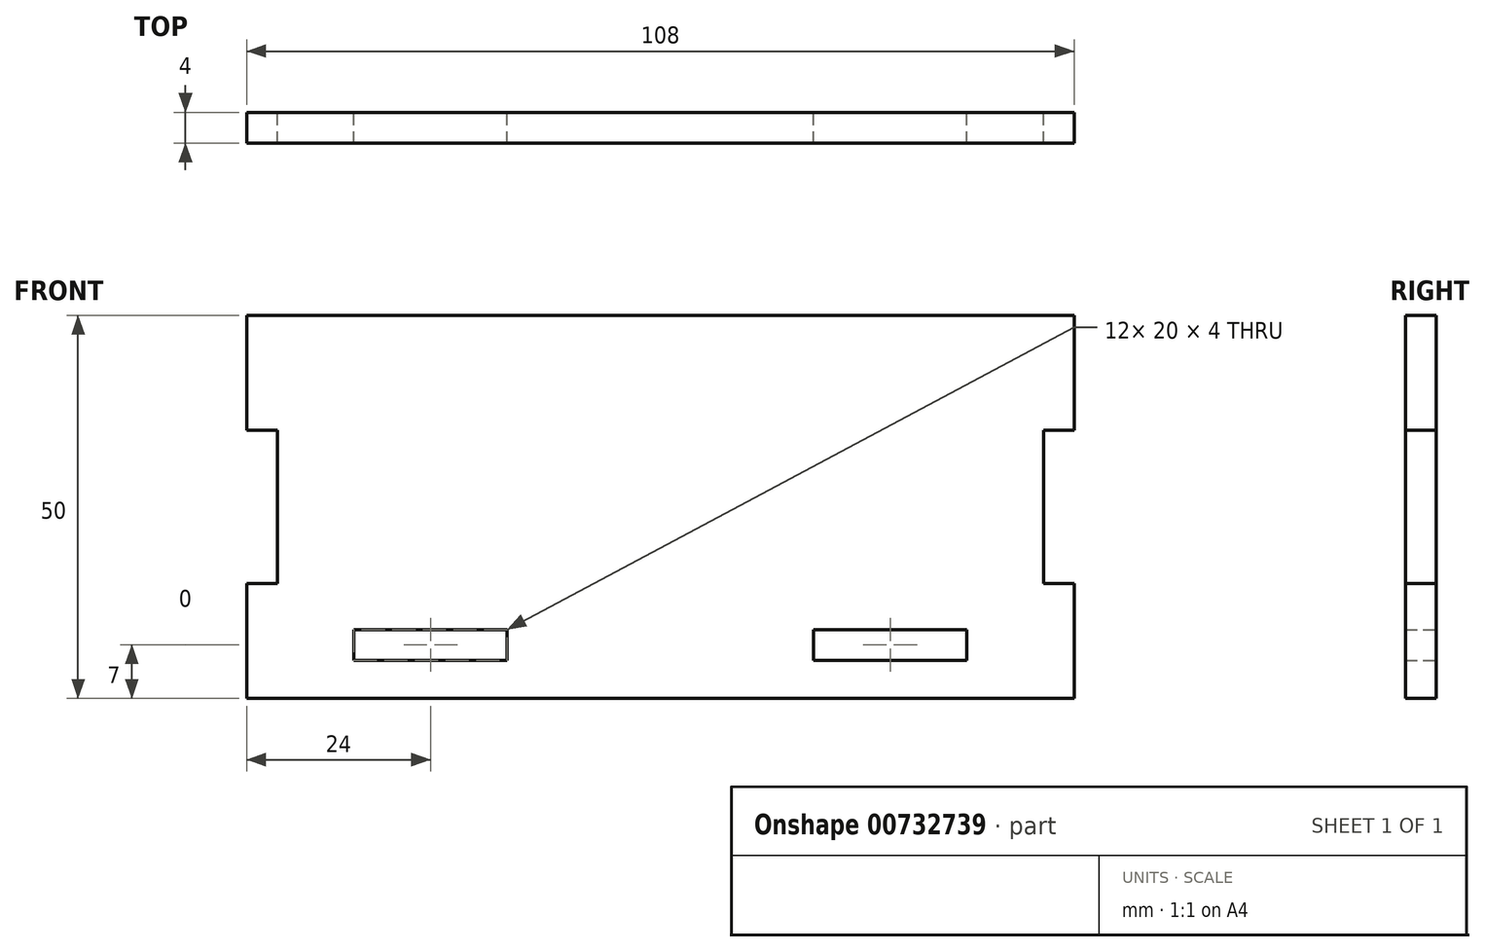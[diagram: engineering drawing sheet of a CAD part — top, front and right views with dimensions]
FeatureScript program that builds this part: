
annotation { "Feature Type Name" : "Feature", "Feature Type Description" : "" }
export const myFeature = defineFeature(function(context is Context, id is Id, definition is map)
    precondition{}
    {
        {
            var Q0;
            Q0=qCreatedBy(makeId("Front.planeOp"),FACE);
            var sketch = newSketch(context, id + "F0", { "sketchPlane" : qUnion([Q0])});
            skLineSegment(sketch, "E0.bottom", {"start": v(54, 25) * mm, "end": v(-54, 25) * mm});
            skLineSegment(sketch, "E0.top", {"start": v(54, -25) * mm, "end": v(-54, -25) * mm});
            skLineSegment(sketch, "E0.left", {"start": v(54, 25) * mm, "end": v(54, 10) * mm});
            skLineSegment(sketch, "E0.right", {"start": v(-54, 25) * mm, "end": v(-54, 10) * mm});
            skPoint(sketch, "E0.middle", {"position": v(0, 0) * mm});
            skLineSegment(sketch, "E1.bottom", {"start": v(-40, -16) * mm, "end": v(-20, -16) * mm});
            skLineSegment(sketch, "E1.top", {"start": v(-40, -20) * mm, "end": v(-20, -20) * mm});
            skLineSegment(sketch, "E1.left", {"start": v(-40, -16) * mm, "end": v(-40, -20) * mm});
            skLineSegment(sketch, "E1.right", {"start": v(-20, -16) * mm, "end": v(-20, -20) * mm});
            skLineSegment(sketch, "E2.MirrorCS", {"start": v(40, -16) * mm, "end": v(20, -16) * mm});
            skLineSegment(sketch, "E3.MirrorCS", {"start": v(40, -20) * mm, "end": v(20, -20) * mm});
            skLineSegment(sketch, "E4.MirrorCS", {"start": v(40, -16) * mm, "end": v(40, -20) * mm});
            skLineSegment(sketch, "E5.MirrorCS", {"start": v(20, -16) * mm, "end": v(20, -20) * mm});
            skLineSegment(sketch, "E6.bottom", {"start": v(-54, 10) * mm, "end": v(-50, 10) * mm});
            skLineSegment(sketch, "E6.top", {"start": v(-54, -10) * mm, "end": v(-50, -10) * mm});
            skLineSegment(sketch, "E6.right", {"start": v(-50, 10) * mm, "end": v(-50, -10) * mm});
            skLineSegment(sketch, "E7.MirrorCS", {"start": v(54, -10) * mm, "end": v(50, -10) * mm});
            skLineSegment(sketch, "E8.MirrorCS", {"start": v(50, 10) * mm, "end": v(50, -10) * mm});
            skLineSegment(sketch, "E9.MirrorCS", {"start": v(54, 10) * mm, "end": v(50, 10) * mm});
            skLineSegment(sketch, "E10.trimOffspring", {"start": v(-54, -10) * mm, "end": v(-54, -25) * mm});
            skLineSegment(sketch, "E11.trimOffspring", {"start": v(54, -10) * mm, "end": v(54, -25) * mm});
            skSolve(sketch);
        }
        {
            var Q0;
            Q0=makeQuery(id+"F0.imprint","IMPRINT",FACE,{"disambiguationData":[TD([[makeQuery(id+"F0.imprint","IMPRINT",EDGE,{"derivedFrom":sQuery(id+"F0.wireOp",EDGE,"E0.bottom")}),1.0]])]});
            extrude(context, id + "F1", {"entities" : qUnion([Q0]), "depth" : 4 * mm, "offsetDistance" : 25 * mm});
        }
    });
